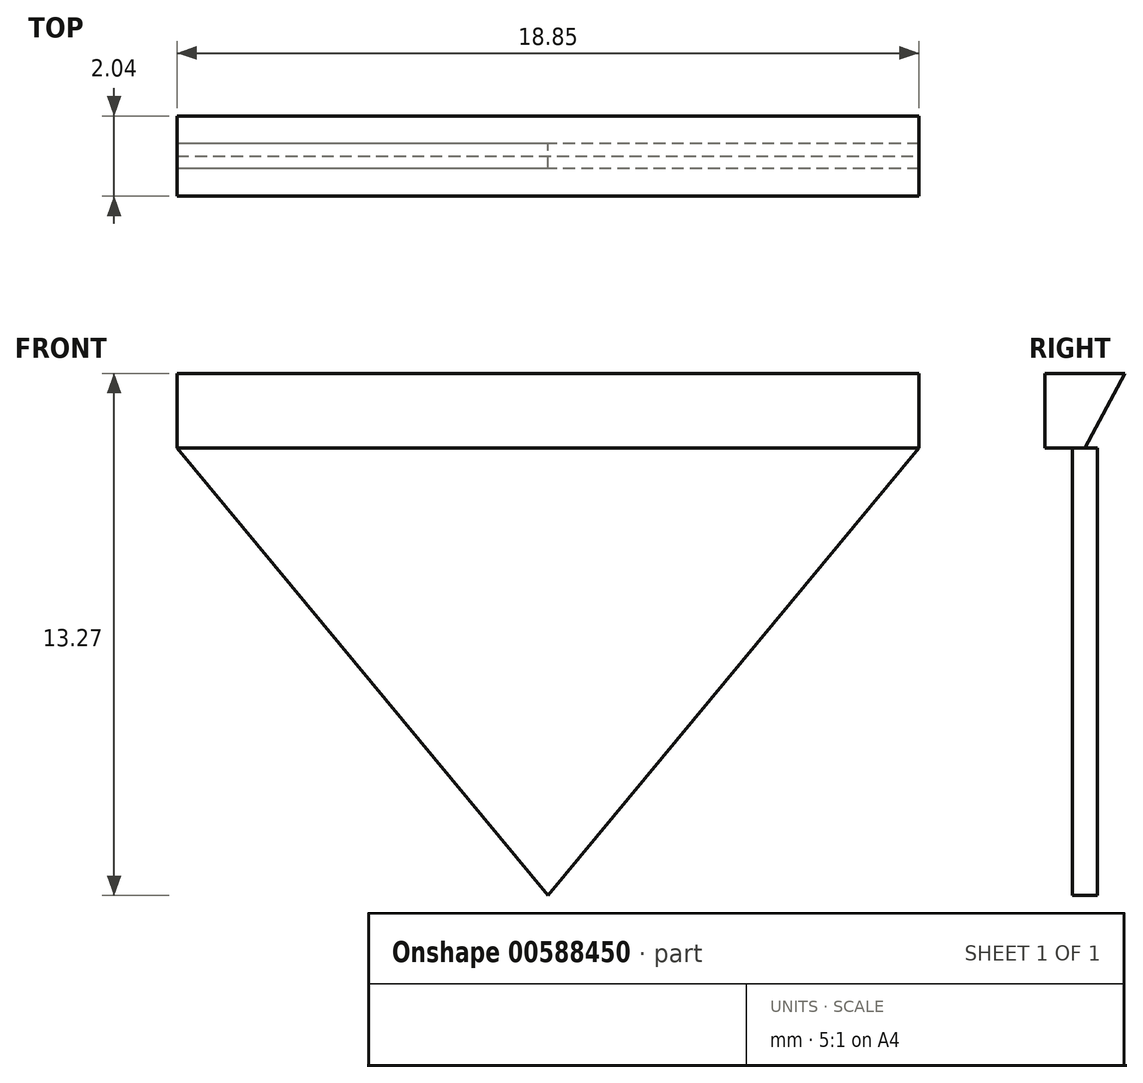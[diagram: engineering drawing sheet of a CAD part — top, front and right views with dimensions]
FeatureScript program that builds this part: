
annotation { "Feature Type Name" : "Feature", "Feature Type Description" : "" }
export const myFeature = defineFeature(function(context is Context, id is Id, definition is map)
    precondition{}
    {
        {
            var Q0;
            Q0=qCreatedBy(makeId("Front.planeOp"),FACE);
            var sketch = newSketch(context, id + "F0", { "sketchPlane" : qUnion([Q0])});
            skLineSegment(sketch, "E0", {"start": v(0, 0) * mm, "end": v(18.85, 0) * mm});
            skLineSegment(sketch, "E1", {"start": v(18.85, 0) * mm, "end": v(18.85, -1.9) * mm});
            skLineSegment(sketch, "E2", {"start": v(18.85, -1.9) * mm, "end": v(0, -1.9) * mm});
            skLineSegment(sketch, "E3", {"start": v(0, -1.9) * mm, "end": v(0, 0) * mm});
            skLineSegment(sketch, "E4", {"start": v(18.85, -1.9) * mm, "end": v(9.43, -13.27) * mm});
            skLineSegment(sketch, "E5", {"start": v(9.43, -13.27) * mm, "end": v(0, -1.9) * mm});
            skPoint(sketch, "E6", {"position": v(9.43, -1.9) * mm});
            skSolve(sketch);
        }
        {
            var Q0;
            Q0=makeQuery(id+"F0.imprint","IMPRINT",FACE,{"disambiguationData":[TD([[makeQuery(id+"F0.imprint","IMPRINT",EDGE,{"derivedFrom":sQuery(id+"F0.wireOp",EDGE,"E0")}),-1.0]])]});
            extrude(context, id + "F1", {"entities" : qUnion([Q0]), "endBound" : BoundingType.SYMMETRIC, "depth" : 2.03 * mm, "offsetDistance" : 25.4 * mm});
        }
        {
            var Q0;
            Q0 = qSketchRegion(id + "F0", true);
            extrude(context, id + "F2", {"entities" : qUnion([Q0]), "operationType" : NewBodyOperationType.ADD, "endBound" : BoundingType.SYMMETRIC, "depth" : 0.64 * mm, "offsetDistance" : 25.4 * mm});
        }
        {
            var Q0;
            Q0=makeQuery(id+"F1.opExtrude","SWEPT_FACE",FACE,{"disambiguationData":[OSD([sQuery(id+"F0.wireOp",EDGE,"E1")])]});
            var sketch = newSketch(context, id + "F3", { "sketchPlane" : qUnion([Q0])});
            skLineSegment(sketch, "E7", {"start": v(1.02, 0) * mm, "end": v(0, -1.9) * mm});
            skLineSegment(sketch, "E8", {"start": v(0, -1.9) * mm, "end": v(1.02, -1.9) * mm});
            skLineSegment(sketch, "E9", {"start": v(1.02, -1.9) * mm, "end": v(1.02, 0) * mm});
            skSolve(sketch);
        }
        {
            var Q0;
            {var subQ0=sQuery(id+"F3.wireOp",EDGE,"E7");Q0=makeQuery(id+"F3.imprint","IMPRINT",FACE,{"disambiguationData":[TD([[makeQuery(id+"F3.imprint","IMPRINT",EDGE,{"derivedFrom":subQ0}),1.0]])]});}
            extrude(context, id + "F4", {"entities" : qUnion([Q0]), "operationType" : NewBodyOperationType.REMOVE, "endBound" : BoundingType.SYMMETRIC, "oppositeDirection" : true, "depth" : 101.6 * mm, "offsetDistance" : 25.4 * mm});
        }
    });
